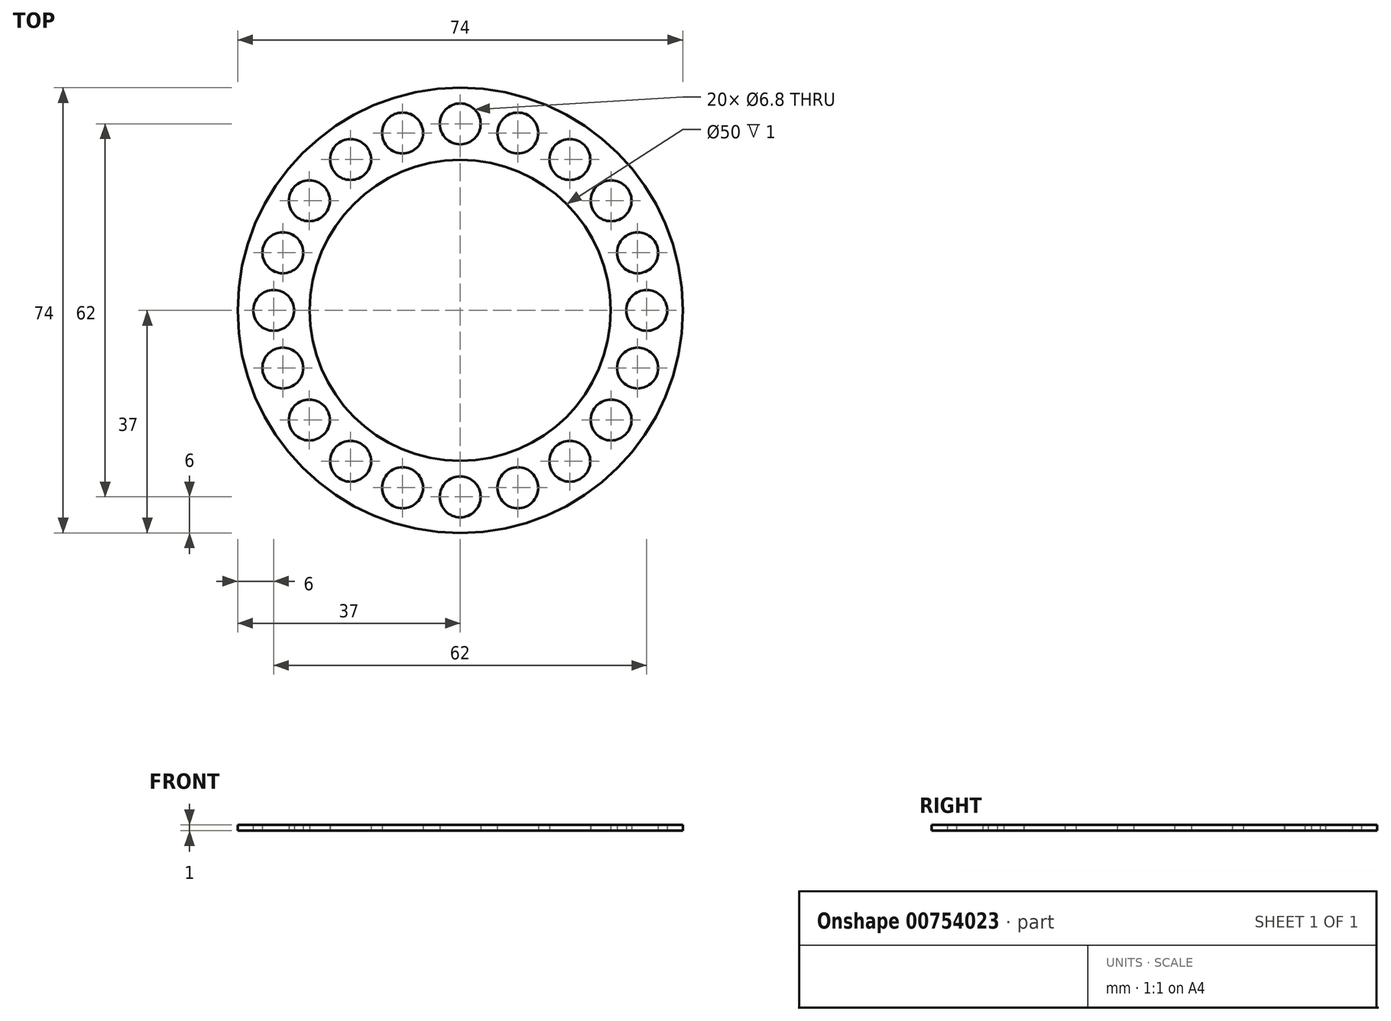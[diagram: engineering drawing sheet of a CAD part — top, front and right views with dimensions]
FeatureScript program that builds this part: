
annotation { "Feature Type Name" : "Feature", "Feature Type Description" : "" }
export const myFeature = defineFeature(function(context is Context, id is Id, definition is map)
    precondition{}
    {
        {
            var Q0;
            Q0=qCreatedBy(makeId("Top.planeOp"),FACE);
            var sketch = newSketch(context, id + "F0", { "sketchPlane" : qUnion([Q0])});
            skCircle(sketch, "E0", {"center": v(0, 0) * mm, "radius": 31 * mm, "construction": true});
            skCircle(sketch, "E1", {"center": v(0, 0) * mm, "radius": 25 * mm});
            skCircle(sketch, "E2", {"center": v(0, 0) * mm, "radius": 37 * mm});
            skCircle(sketch, "E3", {"center": v(0, 31) * mm, "radius": 3.4 * mm});
            skCircle(sketch, "E4.1.0", {"center": v(-9.58, 29.48) * mm, "radius": 3.4 * mm});
            skCircle(sketch, "E4.2.0", {"center": v(-18.22, 25.08) * mm, "radius": 3.4 * mm});
            skCircle(sketch, "E4.3.0", {"center": v(-25.08, 18.22) * mm, "radius": 3.4 * mm});
            skCircle(sketch, "E4.4.0", {"center": v(-29.48, 9.58) * mm, "radius": 3.4 * mm});
            skCircle(sketch, "E4.5.0", {"center": v(-31, 0) * mm, "radius": 3.4 * mm});
            skCircle(sketch, "E4.6.0", {"center": v(-29.48, -9.58) * mm, "radius": 3.4 * mm});
            skCircle(sketch, "E4.7.0", {"center": v(-25.08, -18.22) * mm, "radius": 3.4 * mm});
            skCircle(sketch, "E4.8.0", {"center": v(-18.22, -25.08) * mm, "radius": 3.4 * mm});
            skCircle(sketch, "E4.9.0", {"center": v(-9.58, -29.48) * mm, "radius": 3.4 * mm});
            skCircle(sketch, "E4.10.0", {"center": v(0, -31) * mm, "radius": 3.4 * mm});
            skCircle(sketch, "E4.11.0", {"center": v(9.58, -29.48) * mm, "radius": 3.4 * mm});
            skCircle(sketch, "E4.12.0", {"center": v(18.22, -25.08) * mm, "radius": 3.4 * mm});
            skCircle(sketch, "E4.13.0", {"center": v(25.08, -18.22) * mm, "radius": 3.4 * mm});
            skCircle(sketch, "E4.14.0", {"center": v(29.48, -9.58) * mm, "radius": 3.4 * mm});
            skCircle(sketch, "E4.15.0", {"center": v(31, 0) * mm, "radius": 3.4 * mm});
            skCircle(sketch, "E4.16.0", {"center": v(29.48, 9.58) * mm, "radius": 3.4 * mm});
            skCircle(sketch, "E4.17.0", {"center": v(25.08, 18.22) * mm, "radius": 3.4 * mm});
            skCircle(sketch, "E4.18.0", {"center": v(18.22, 25.08) * mm, "radius": 3.4 * mm});
            skCircle(sketch, "E4.19.0", {"center": v(9.58, 29.48) * mm, "radius": 3.4 * mm});
            skSolve(sketch);
        }
        {
            var Q0;
            Q0 = qSketchRegion(id + "F0", true);
            extrude(context, id + "F1", {"entities" : qUnion([Q0]), "depth" : 1 * mm, "offsetDistance" : 25 * mm});
        }
    });
